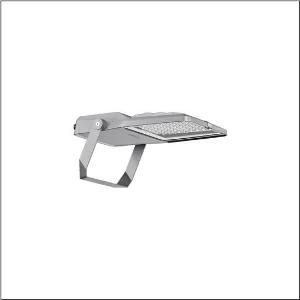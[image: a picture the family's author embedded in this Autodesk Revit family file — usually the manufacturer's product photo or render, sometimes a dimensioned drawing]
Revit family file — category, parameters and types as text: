
# Revit family: floodlight_fl_21_mini___pl61_5xa7776b2c1a_e1cc
name_source: partatom
category: Lighting Fixtures
units: mm (PartAtom-declared; Revit-internal decimal feet)

## family parameters
Cut with Voids When Loaded = No
Host = Face
Light Source = No
Part Type = Normal
Room Calculation Point = No
Round Connector Dimension = Use Diameter
Shared = No

## types (1)
- --- (1 x LED, 6110 lm, 45.7 W, 3000K)
    Apparent Load = 46 VA
    CIE Flux Codes = 33 65 98 100 100
    Color Rendering = 70
    Color Temperature = 3000K
    Default Elevation = 1800 mm
    Description = Floodlight FL 21 mini, floodlight, primary light control with lens, of PMMA, primary optical cover: protective disc, of toughened safety glass, transparent, light distribution: PL61, light emission: direct distribution, installation type: surface-mounted, LED, High Power LED, rated luminous flux: 6.110lm, luminous efficacy: 134lm/W, light colour: 730, colour temperature: 3000K, control: flexible luminous flux parameterisation, time-dependent luminous flux control, constant luminous flux control, overheat protection, presetting dimming logarithmic, with terminal, 6-pole, mains connection: 220..240V, AC, 50/60Hz, start of lifetime: 46W, end of service life: 48W, reduction: 22W, luminaire housing, of diecast aluminium, powder-coated, Siteco® metallic grey (DB 702S), corrosivity category C5 mid according to DIN EN ISO 12944, sealing non-destructively replaceable, mounting bracket, of steel, galvanised, powder-coated, Siteco® metallic grey (DB 702S), Smart Interface below and above, protection rating (complete): IP66, insulation class (complete): insulation class II (safety insulation), certification: CE, ENEC, VDE, protection symbol: D, impact resistance: IK08, permissible operating ambient temperature: -40..+40°C, permissible operating ambient temperature for outdoor applications: -40..+50°C, standard: DIN EN 12944, LABS conformity tested according to VDMA 24364:2018-05, packaging unit: 1 piece

Light Distribution: PL61
    Height = 70 mm
    Lamp = 1 x LED
    Lamp Light Flux = 6110 lm
    Lamp Power = 45.7 W
    Lamp count = 1
    Length = 485 mm
    Luminous efficacy = 134 lm/W
    Manufacturer = Siteco
    ModVariant = No
    Model = 5XA7776B2C1A
    Number of Poles = 1
    OnlyDefault = Yes
    Power Factor = 1
    Product Name = Floodlight FL 21 mini | PL61
    Product group = floodlight | pylon annexe
    ProductGroupID = 6200
    Protection Class = Protection class II
    Protection Degree = IP 66
    RLX_Detail_Level = 1
    RLX_Emergency_Light_Flux = 0 lm
    RLX_Emergency_Type = 0
    RLX_Emergency_Type_DB = No
    RlxData = <blob elided: 95869 chars, md5=e9a607a3>
    Socket = socket
    Standby Power = 0 W
    System Light Flux = 6110 lm
    System Power = 46 W
    Type Comments = factory setting: luminous flux: 100 % | dim-lin: 254 | 463 mA
    Type Image = l_1006845.jpg
    URL = http://relux.com
    VarID = @adj_123087
    Voltage = 0 V
    Weight = 0.00 kg
    Width = 337 mm

## geometry (parser evidence)
native form markers: Blend x4, Sweep x11
no freeform markers — native parametric forms only
